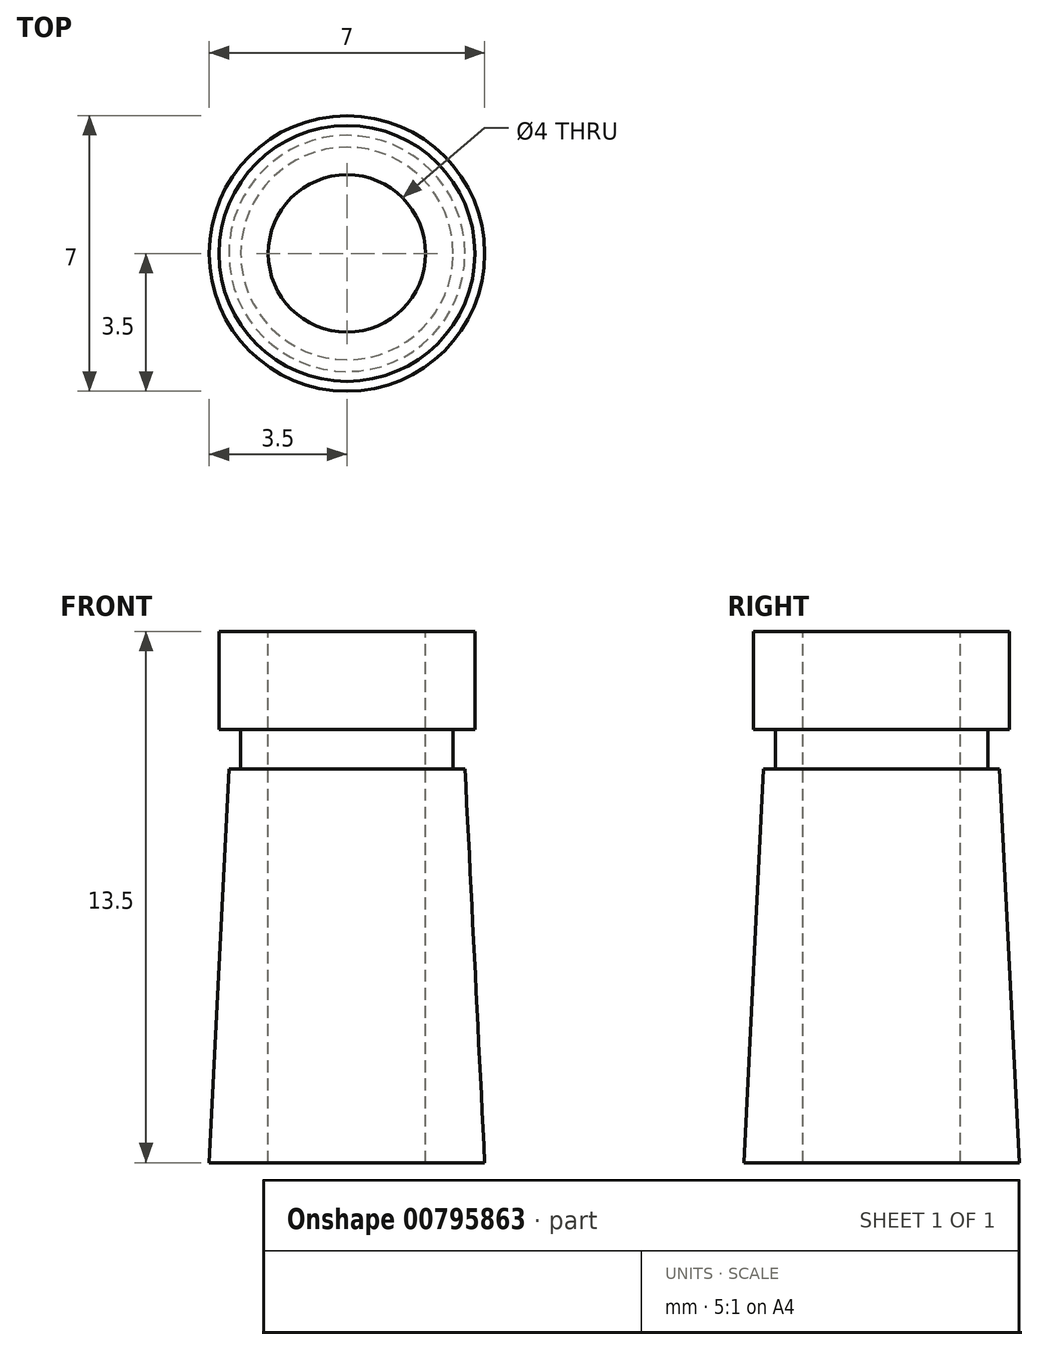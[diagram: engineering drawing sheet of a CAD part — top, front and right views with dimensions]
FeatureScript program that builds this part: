
annotation { "Feature Type Name" : "Feature", "Feature Type Description" : "" }
export const myFeature = defineFeature(function(context is Context, id is Id, definition is map)
    precondition{}
    {
        {
            var Q0;
            Q0=qCreatedBy(makeId("Front.planeOp"),FACE);
            var sketch = newSketch(context, id + "F0", { "sketchPlane" : qUnion([Q0])});
            skLineSegment(sketch, "E0", {"start": v(3.5, 0) * mm, "end": v(3, 10) * mm});
            skLineSegment(sketch, "E1", {"start": v(3, 10) * mm, "end": v(2.7, 10) * mm});
            skLineSegment(sketch, "E2", {"start": v(2.7, 10) * mm, "end": v(2.7, 11) * mm});
            skLineSegment(sketch, "E3", {"start": v(2.7, 11) * mm, "end": v(3.25, 11) * mm});
            skLineSegment(sketch, "E4", {"start": v(3.25, 11) * mm, "end": v(3.25, 13.5) * mm});
            skLineSegment(sketch, "E5", {"start": v(3.25, 13.5) * mm, "end": v(2, 13.5) * mm});
            skLineSegment(sketch, "E6", {"start": v(2, 13.5) * mm, "end": v(2, 0) * mm});
            skLineSegment(sketch, "E7", {"start": v(2, 0) * mm, "end": v(3.5, 0) * mm});
            skLineSegment(sketch, "E8", {"start": v(0, 13.27) * mm, "end": v(0, 0) * mm, "construction": true});
            skSolve(sketch);
        }
        {
            var Q0;
            Q0 = qSketchRegion(id + "F0", true);
            var Q1;
            Q1=sQuery(id+"F0.wireOp",EDGE,"E8");
            revolve(context, id + "F1", {"surfaceOperationType" : NewSurfaceOperationType.NEW, "entities" : qUnion([Q0]), "axis" : qUnion([Q1]), "revolveType" : RevolveType.FULL});
        }
    });
